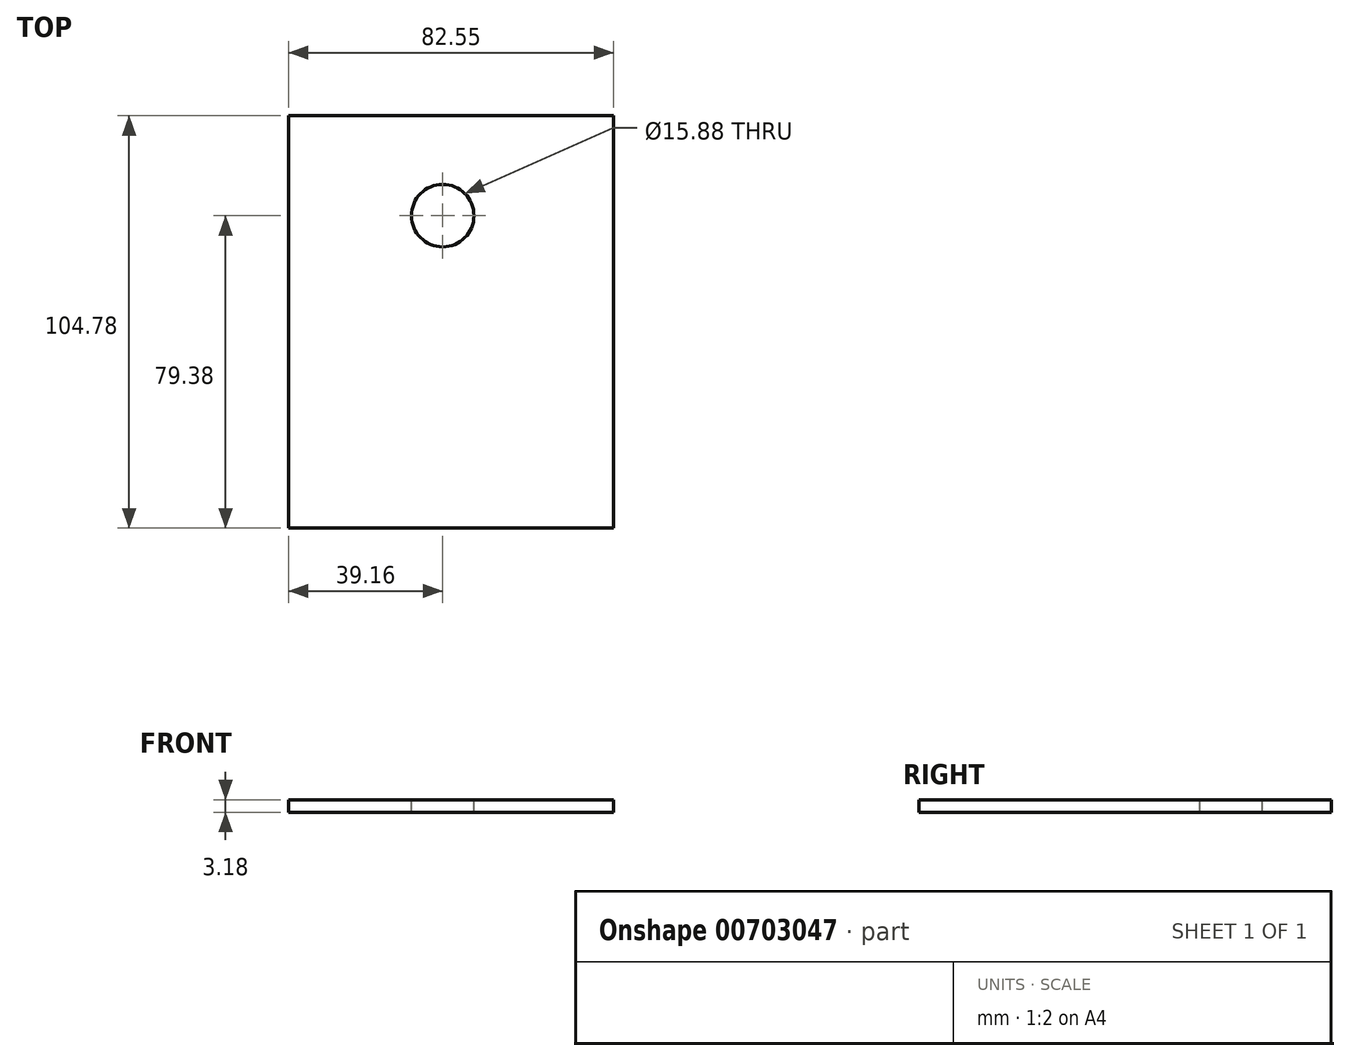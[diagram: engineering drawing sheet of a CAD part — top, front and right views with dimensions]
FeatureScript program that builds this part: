
annotation { "Feature Type Name" : "Feature", "Feature Type Description" : "" }
export const myFeature = defineFeature(function(context is Context, id is Id, definition is map)
    precondition{}
    {
        {
            var Q0;
            Q0=qCreatedBy(makeId("Top.planeOp"),FACE);
            var sketch = newSketch(context, id + "F0", { "sketchPlane" : qUnion([Q0])});
            skLineSegment(sketch, "E0.bottom", {"start": v(-39.16, 25.4) * mm, "end": v(43.39, 25.4) * mm});
            skLineSegment(sketch, "E0.top", {"start": v(-39.16, -79.37) * mm, "end": v(43.39, -79.37) * mm});
            skLineSegment(sketch, "E0.left", {"start": v(-39.16, 25.4) * mm, "end": v(-39.16, -79.37) * mm});
            skLineSegment(sketch, "E0.right", {"start": v(43.39, 25.4) * mm, "end": v(43.39, -79.37) * mm});
            skSolve(sketch);
        }
        {
            var Q0;
            Q0=qSketchRegion(id+"FR5LTdiXmvA82zs_1",true);
            var Q1;
            Q1=qSketchRegion(id+"F0",true);
            extrude(context, id + "F1", {"entities" : qUnion([Q0, Q1]), "depth" : 3.17 * mm, "offsetDistance" : 25.4 * mm});
        }
        {
            var Q0;
            Q0=makeQuery(id+"F1.opExtrude","CAP_FACE",FACE,{"disambiguationData":[OSD([sQuery(id+"F0.wireOp",EDGE,"E0.bottom"),sQuery(id+"F0.wireOp",EDGE,"E0.top"),sQuery(id+"F0.wireOp",EDGE,"E0.left"),sQuery(id+"F0.wireOp",EDGE,"E0.right")])],"isStart":false});
            var sketch = newSketch(context, id + "F2", { "sketchPlane" : qUnion([Q0])});
            skCircle(sketch, "E1", {"center": v(0, 0) * mm, "radius": 7.94 * mm});
            skSolve(sketch);
        }
        {
            var Q0;
            Q0=makeQuery(id+"F2.imprint","IMPRINT",FACE,{"disambiguationData":[TD([[makeQuery(id+"F2.imprint","IMPRINT",EDGE,{"derivedFrom":sQuery(id+"F2.wireOp",EDGE,"E1")}),1.0]])]});
            var Q1;
            Q1=sQuery(id+"F2.wireOp",EDGE,"E1");
            extrude(context, id + "F3", {"entities" : qUnion([Q0]), "operationType" : NewBodyOperationType.REMOVE, "surfaceEntities" : qUnion([Q1]), "oppositeDirection" : true, "depth" : 25.4 * mm, "offsetDistance" : 25.4 * mm});
        }
    });
